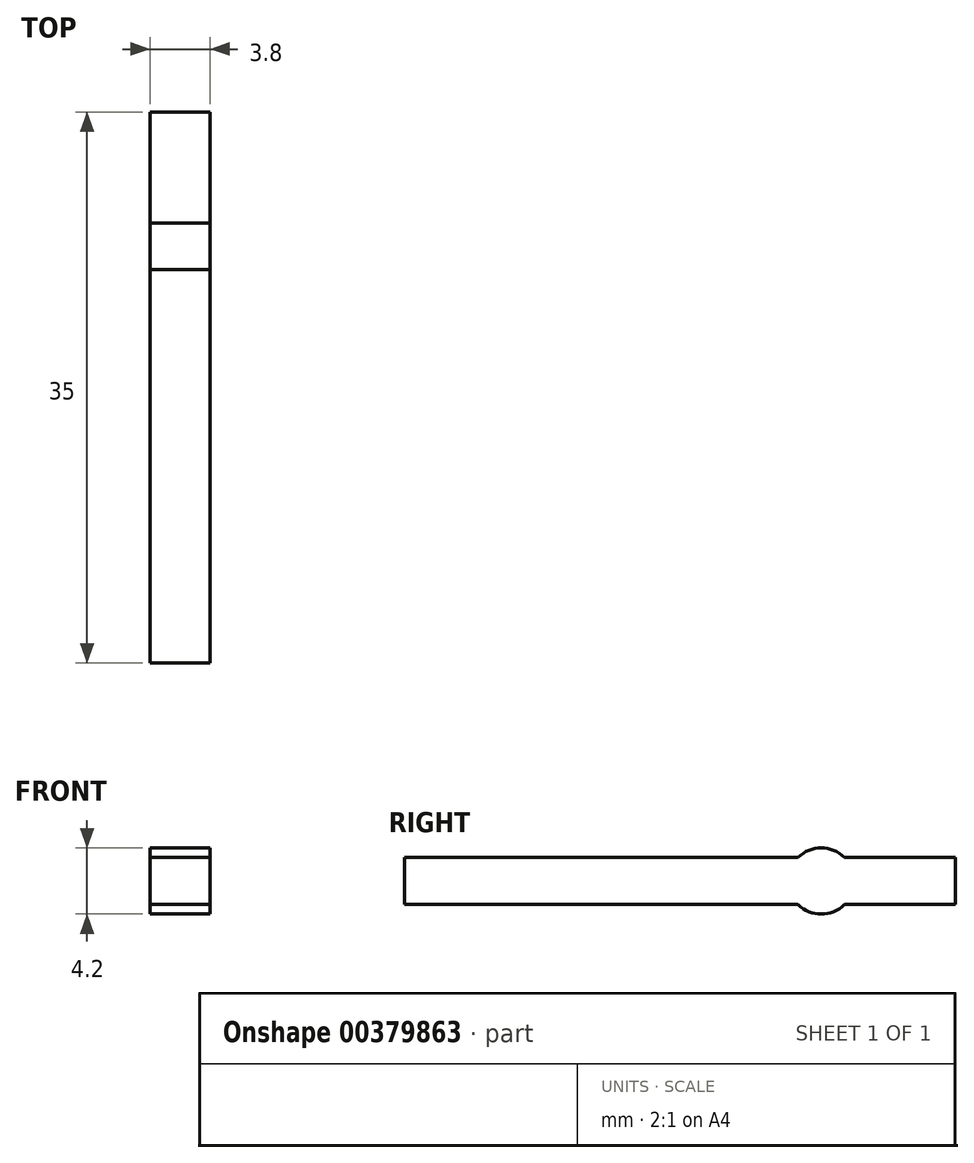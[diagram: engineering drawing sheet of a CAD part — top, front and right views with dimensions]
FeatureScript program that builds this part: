
annotation { "Feature Type Name" : "Feature", "Feature Type Description" : "" }
export const myFeature = defineFeature(function(context is Context, id is Id, definition is map)
    precondition{}
    {
        {
            var Q0;
            Q0=qCreatedBy(makeId("Right.planeOp"),FACE);
            var sketch = newSketch(context, id + "F0", { "sketchPlane" : qUnion([Q0])});
            skCircle(sketch, "E0", {"center": v(0, 0) * mm, "radius": 2.1 * mm});
            skLineSegment(sketch, "E1", {"start": v(-1.47, -1.5) * mm, "end": v(-26.47, -1.5) * mm});
            skLineSegment(sketch, "E2", {"start": v(-1.47, 1.5) * mm, "end": v(-26.47, 1.5) * mm});
            skLineSegment(sketch, "E3", {"start": v(-26.47, 1.5) * mm, "end": v(-26.47, -1.5) * mm});
            skLineSegment(sketch, "E4", {"start": v(-1.47, 1.5) * mm, "end": v(8.53, 1.5) * mm});
            skLineSegment(sketch, "E5", {"start": v(8.53, 1.5) * mm, "end": v(8.53, -1.5) * mm});
            skLineSegment(sketch, "E6", {"start": v(8.53, -1.5) * mm, "end": v(-1.47, -1.5) * mm});
            skLineSegment(sketch, "E7", {"start": v(8.53, -1.5) * mm, "end": v(8.53, -4.5) * mm});
            skLineSegment(sketch, "E8", {"start": v(8.53, -4.5) * mm, "end": v(5.53, -4.5) * mm});
            skLineSegment(sketch, "E9", {"start": v(5.53, -4.5) * mm, "end": v(5.53, -1.5) * mm});
            skLineSegment(sketch, "E10", {"start": v(5.53, -1.5) * mm, "end": v(5.53, 1.5) * mm});
            skSolve(sketch);
        }
        {
            var Q0;
            {var subQ0=sQuery(id+"F0.wireOp",EDGE,"E4");var subQ1=sQuery(id+"F0.wireOp",EDGE,"E0");var subQ3=makeQuery(id+"F0.imprint","INTERSECT",VERTEX,{"derivedFrom":[subQ1,subQ0]});Q0=makeQuery(id+"F0.imprint","IMPRINT",FACE,{"disambiguationData":[TD([[makeQuery(id+"F0.imprint","IMPRINT",EDGE,{"disambiguationData":[TD([[subQ3,-1.0]])],"derivedFrom":subQ1}),1.0]])]});}
            var Q1;
            {var subQ0=sQuery(id+"F0.wireOp",EDGE,"E6");var subQ1=sQuery(id+"F0.wireOp",EDGE,"E0");var subQ3=makeQuery(id+"F0.imprint","INTERSECT",VERTEX,{"derivedFrom":[subQ1,subQ0]});Q1=makeQuery(id+"F0.imprint","IMPRINT",FACE,{"disambiguationData":[TD([[makeQuery(id+"F0.imprint","IMPRINT",EDGE,{"disambiguationData":[TD([[subQ3,1.0]])],"derivedFrom":subQ1}),1.0]])]});}
            var Q2;
            {var subQ5=sQuery(id+"F0.wireOp",EDGE,"E10");Q2=makeQuery(id+"F0.imprint","IMPRINT",FACE,{"disambiguationData":[TD([[makeQuery(id+"F0.imprint","IMPRINT",EDGE,{"derivedFrom":subQ5}),1.0]])]});}
            var Q3;
            {var subQ0=sQuery(id+"F0.wireOp",EDGE,"E5");Q3=makeQuery(id+"F0.imprint","IMPRINT",FACE,{"disambiguationData":[TD([[makeQuery(id+"F0.imprint","IMPRINT",EDGE,{"derivedFrom":subQ0}),-1.0]])]});}
            var Q4;
            {var subQ1=sQuery(id+"F0.wireOp",EDGE,"E0");var subQ3=sQuery(id+"F0.wireOp",EDGE,"E4");var subQ5=makeQuery(id+"F0.imprint","INTERSECT",VERTEX,{"derivedFrom":[subQ1,subQ3]});Q4=makeQuery(id+"F0.imprint","IMPRINT",FACE,{"disambiguationData":[TD([[makeQuery(id+"F0.imprint","IMPRINT",EDGE,{"disambiguationData":[TD([[subQ5,1.0]])],"derivedFrom":subQ1}),1.0]])]});}
            var Q5;
            {var subQ0=sQuery(id+"F0.wireOp",EDGE,"E1");Q5=makeQuery(id+"F0.imprint","IMPRINT",FACE,{"disambiguationData":[TD([[makeQuery(id+"F0.imprint","IMPRINT",EDGE,{"derivedFrom":subQ0}),-1.0]])]});}
            extrude(context, id + "F1", {"entities" : qUnion([Q0, Q1, Q2, Q3, Q4, Q5]), "depth" : 1.9 * mm, "hasSecondDirection" : true, "secondDirectionOppositeDirection" : true, "secondDirectionDepth" : 1.9 * mm});
        }
    });
